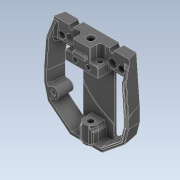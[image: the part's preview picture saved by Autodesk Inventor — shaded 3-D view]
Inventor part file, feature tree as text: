
AUTODESK INVENTOR PART (.ipt)
format: ipt  version: 2022.1 (Build 261234020, 234B)  size: 2,570,752 bytes
history: native  units: mm
features: delete_face x34, sketch x19, reference x19, projected_geometry x17, extrude x16, fillet x14, chamfer x13, other x12, direct_edit x4, move_body x4, hole x3, plane x2, imported_body x1
ambient origin geometry x8: Origin, YZ Plane, XZ Plane, XY Plane, X Axis, Y Axis, Z Axis, Center Point
bodies: Volumenkörper1 (feature_tree)
feature tree (158):
  hole  "Bohrung1"  [1 undecoded]
  delete_face  "Fläche löschen1"
  direct_edit  "Direktbearbeitung1"
  delete_face  "Fläche löschen2"
  delete_face  "Fläche löschen3"
  delete_face  "Fläche löschen4"
  delete_face  "Fläche löschen5"
  delete_face  "Fläche löschen6"
  delete_face  "Fläche löschen7"
  delete_face  "Fläche löschen8"
  delete_face  "Fläche löschen9"
  delete_face  "Fläche löschen10"
  direct_edit  "Direktbearbeitung2"
  fillet  "Rundung1"  Radius=1.0mm
  chamfer  "Fase1"  Distance=0.8mm Angle=45.0deg
  direct_edit  "Direktbearbeitung3"
  delete_face  "Fläche löschen11"
  delete_face  "Fläche löschen12"
  extrude  "Extrusion1"  Depth=10.0mm TaperAngle=0.0deg
  plane  "Arbeitsebene1"
  extrude  "Extrusion2"  Depth=7.6mm
  chamfer  "Fase2"  Distance=3.5mm
  extrude  "Extrusion3"  Depth=7.5mm
  delete_face  "Fläche löschen13"
  extrude  "Extrusion4"  Depth=10.0mm TaperAngle=0.0deg
  chamfer  "Fase3"  Distance=10.0mm
  fillet  "Rundung2"  Radius=1.0mm
  fillet  "Rundung3"  Radius=1.0mm
  extrude  "Extrusion5"  Depth=0.6mm
  chamfer  "Fase4"  [1 undecoded]
  extrude  "Extrusion6"  Depth=6.2mm
  chamfer  "Fase5"  [1 undecoded]
  extrude  "Extrusion7"  Depth=0.4mm TaperAngle=0.0deg
  fillet  "Rundung4"  Radius=0.1mm
  extrude  "Extrusion8"  Depth=0.4mm TaperAngle=0.0deg
  fillet  "Rundung5"  Radius=0.4mm
  delete_face  "Fläche löschen14"
  delete_face  "Fläche löschen15"
  extrude  "Extrusion9"  Depth=10.0mm
  delete_face  "Fläche löschen16"
  extrude  "Extrusion10"  Depth=10.0mm TaperAngle=45.0deg
  chamfer  "Fase6"  Distance=0.4mm Angle=45.0deg
  delete_face  "Fläche löschen17"
  fillet  "Rundung6"  Radius=7.6mm
  hole  "Bohrung2"  [1 undecoded]
  fillet  "Rundung7"  Radius=0.6mm
  chamfer  "Fase7"  [1 undecoded]
  extrude  "Extrusion11"  Depth=1.0mm
  chamfer  "Fase8"  Distance=1.0mm
  direct_edit  "Direktbearbeitung4"
  delete_face  "Fläche löschen18"
  plane  "Arbeitsebene2"
  extrude  "Extrusion12"  Depth=1.0mm
  fillet  "Rundung8"  Radius=2.0mm
  fillet  "Rundung9"  Radius=1.0mm
  fillet  "Rundung10"  Radius=9.81mm
  delete_face  "Fläche löschen19"
  delete_face  "Fläche löschen20"
  extrude  "Extrusion13"  TaperAngle=0.0deg  [1 undecoded]
  delete_face  "Fläche löschen21"
  delete_face  "Fläche löschen22"
  delete_face  "Fläche löschen23"
  sketch  "Skizze16"  dims[d70=3.8mm d71=6.0mm d72=4.0mm d73=2.0mm d74=90.0deg d75=8.0mm d76=20.594885mm]
  delete_face  "Fläche löschen24"
  extrude  "Extrusion14"  Depth=10.0mm TaperAngle=0.0deg
  delete_face  "Fläche löschen25"
  extrude  "Extrusion15"  Depth=10.0mm TaperAngle=0.0deg
  delete_face  "Fläche löschen26"
  delete_face  "Fläche löschen27"
  chamfer  "Fase9"  Distance=0.4mm
  delete_face  "Fläche löschen28"
  delete_face  "Fläche löschen29"
  delete_face  "Fläche löschen30"
  delete_face  "Fläche löschen31"
  fillet  "Rundung11"  Radius=2.0mm
  fillet  "Rundung12"  Radius=4.0mm
  fillet  "Rundung13"  Radius=1.0mm
  delete_face  "Fläche löschen32"
  chamfer  "Fase10"  Distance=0.4mm
  extrude  "Extrusion16"  TaperAngle=0.0deg  [1 undecoded]
  chamfer  "Fase11"  Distance=0.4mm
  chamfer  "Fase12"  Distance=0.4mm
  delete_face  "Fläche löschen33"
  delete_face  "Fläche löschen34"
  hole  "Bohrung3"  [1 undecoded]
  chamfer  "Fase13"  Distance=1.0mm
  fillet  "Rundung14"  [1 undecoded]
  sketch  "Skizze1"  dims[d0=4.12mm d1=6.0mm d2=4.0mm d3=2.0mm d4=90.0deg d5=5.0mm d6=20.594885mm d7=0.0mm d8=0.0mm d9=9.5mm]
  reference  "Referenz1"
  reference  "Referenz2"
  reference  "Referenz3"
  reference  "Referenz4"
  sketch  "Skizze2"  dims[d10=0.0mm d11=0.0mm d12=0.777mm d13=1.0mm d14=0.8mm d15=2.0mm d16=45.0deg]
  projected_geometry  "Projizierte Kontur1"
  projected_geometry  "Projizierte Kontur2"
  sketch  "Skizze3"  dims[d17=0.0mm d18=2.25mm d19=0.0mm d20=10.0mm d21=0.0mm]
  sketch  "Skizze4"  dims[d22=-10.5mm d23=7.6mm d24=3.5mm d25=0.0mm]
  projected_geometry  "Projizierte Kontur3"
  sketch  "Skizze5"  dims[d26=0.4mm d27=2.0mm d28=45.0deg d29=7.5mm]
  projected_geometry  "Projizierte Kontur4"
  sketch  "Skizze6"  dims[d30=1.21mm d31=3.5mm d32=0.0mm d33=10.0mm d34=0.0mm]
  reference  "Referenz5"
  sketch  "Skizze7"  dims[d35=0.4mm d36=2.0mm d37=45.0deg d38=1.0mm d39=1.0mm]
  sketch  "Skizze8"  dims[d40=0.4mm d41=0.6mm]
  reference  "Referenz6"
  reference  "Referenz7"
  reference  "Referenz8"
  reference  "Referenz9"
  reference  "Referenz10"
  reference  "Referenz11"
  reference  "Referenz12"
  reference  "Referenz13"
  reference  "Referenz14"
  reference  "Referenz15"
  reference  "Referenz16"
  sketch  "Skizze9"  dims[d42=1.0mm d43=0.0mm d44=0.0mm]
  projected_geometry  "Projizierte Kontur5"
  sketch  "Skizze10"  dims[d45=0.4mm d46=2.0mm d47=45.0deg d48=6.2mm d49=0.0mm d50=0.0mm]
  projected_geometry  "Projizierte Kontur6"
  sketch  "Skizze11"  dims[d51=0.4mm d52=2.0mm d53=45.0deg d54=0.4mm d55=0.0mm d56=0.1mm]
  projected_geometry  "Projizierte Kontur7"
  sketch  "Skizze12"  dims[d57=0.8mm d58=0.4mm d59=0.0mm d60=0.4mm]
  reference  "Referenz17"
  reference  "Referenz18"
  reference  "Referenz19"
  sketch  "Skizze13"  dims[d61=10.0mm d62=0.0mm d63=0.8mm]
  projected_geometry  "Projizierte Kontur8"
  sketch  "Skizze14"  dims[d64=10.0mm d65=0.0mm d66=0.4mm d67=2.0mm d68=45.0deg]
  projected_geometry  "Projizierte Kontur9"
  sketch  "Skizze15"  dims[d69=1.0mm]
  projected_geometry  "Projizierte Kontur10"
  projected_geometry  "Projizierte Kontur11"
  projected_geometry  "Projizierte Kontur12"
  projected_geometry  "Projizierte Kontur13"
  projected_geometry  "Projizierte Kontur14"
  projected_geometry  "Projizierte Kontur15"
  sketch  "Skizze17"  dims[d77=0.2mm d78=0.4mm d79=2.0mm d80=45.0deg d81=7.6mm]
  projected_geometry  "Projizierte Kontur16"
  sketch  "Skizze18"  dims[d82=8.2mm d83=10.0mm d84=0.0mm]
  projected_geometry  "Projizierte Kontur17"
  sketch  "Skizze19"  dims[d85=1.6mm d86=2.0mm d87=4.4mm d88=0.0mm d89=0.0mm d90=0.6mm d91=-3.0mm d92=12.0mm d93=1.0mm d94=0.0mm d95=2.0mm d96=2.0mm d97=1.0mm d98=9.81mm d99=0.0mm d100=0.0mm d101=10.0mm d102=0.0mm d103=10.0mm d104=0.0mm d105=0.4mm d106=2.0mm d107=4.4mm d108=2.0mm d109=4.0mm d110=1.0mm d111=0.4mm d112=2.0mm d113=4.4mm d114=0.0mm d115=0.0mm d116=0.4mm d117=2.0mm d118=4.4mm d119=0.4mm d120=2.0mm d121=4.4mm d122=4.2mm d123=6.0mm d124=3.6mm d125=7.0mm d126=90.0deg d127=8.0mm d128=0.0mm d129=0.8mm d130=2.0mm d131=45.0deg d132=1.0mm]
  imported_body  "Basis1"
  other  "<userpath>\Desktop\RAMA_SBNG\Toolheads.iam"
  other  "Toolheads.iam"
  other  "stealthburner_toolhead_(revo_voron)-front-beta2:1"
  other  "stealthburner_toolhead_(revo_voron)-rear-cw2-beta2 (1):1"
  move_body  "Verschieben1"
  move_body  "Verschieben2"
  move_body  "Verschieben3"
  other  "<userpath>\Desktop\RAMA_SBNG\LGX_Lite_Stealthburner_Normal.iam"
  other  "LGX_Lite_Stealthburner_Normal.iam"
  other  "2PC-SB-PCB:1"
  other  "Component39:1"
  other  "LGX-Lite Dummy"
  other  "Rear_body_LGX_Lite_Stealthburner_rev01"
  other  "X_Right:1"
  other  "X_Left:1"
  move_body  "Verschieben4"
note: 9 required parameter values undecoded (feature->parameter linkage not recoverable at this tier; creation-order binding heuristic only, values carry confidence <= 0.55)
